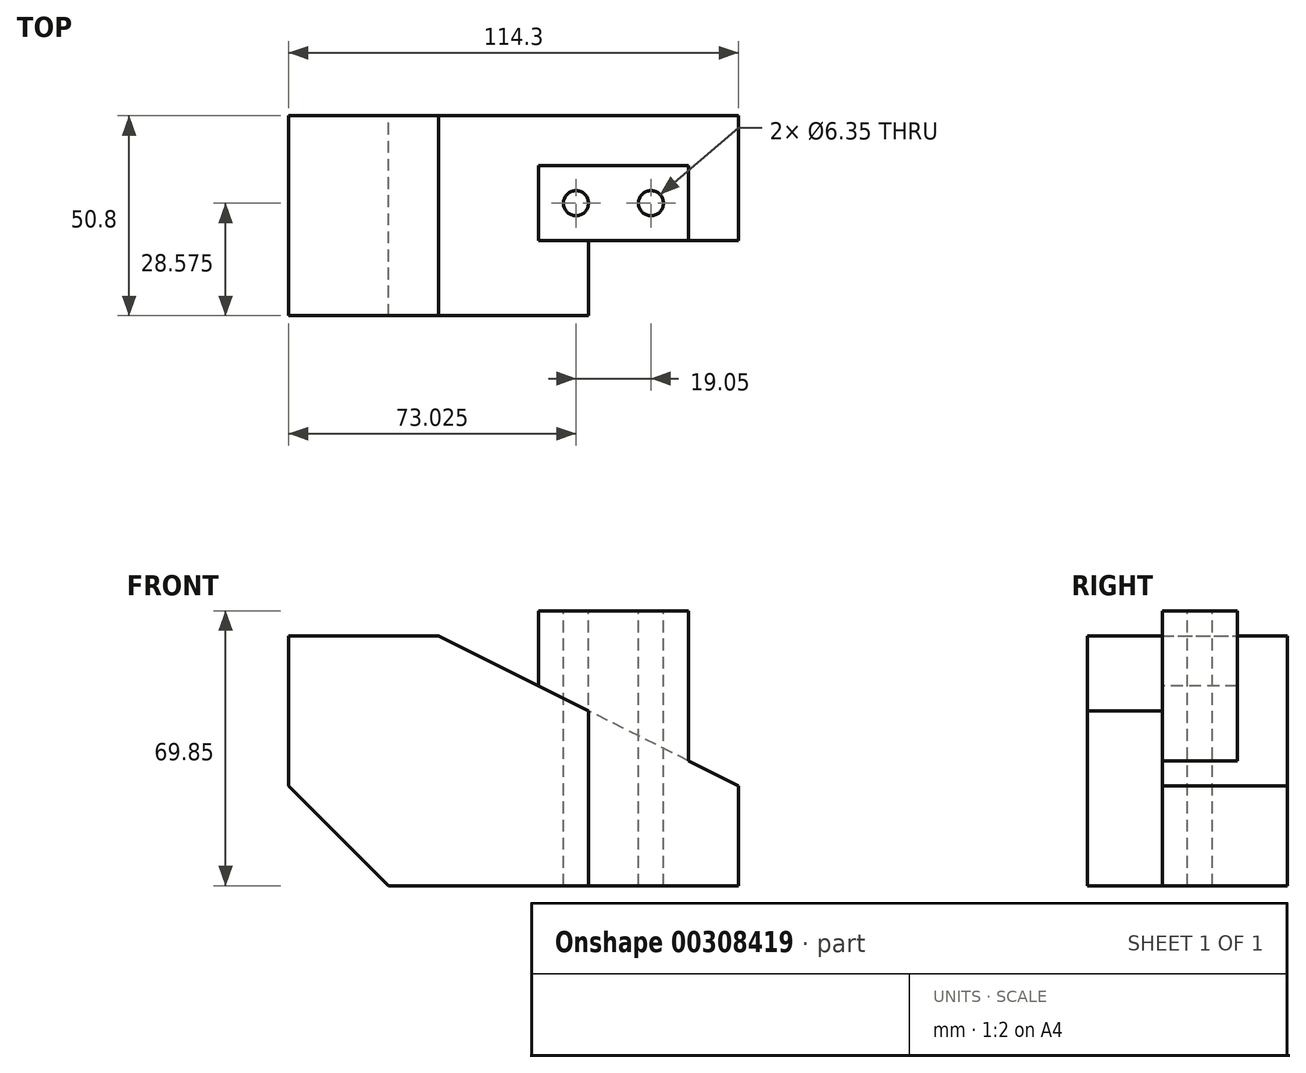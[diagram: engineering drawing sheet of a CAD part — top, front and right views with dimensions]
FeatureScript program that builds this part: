
annotation { "Feature Type Name" : "Feature", "Feature Type Description" : "" }
export const myFeature = defineFeature(function(context is Context, id is Id, definition is map)
    precondition{}
    {
        {
            var Q0;
            Q0=qCreatedBy(makeId("Front.planeOp"),FACE);
            var sketch = newSketch(context, id + "F0", { "sketchPlane" : qUnion([Q0])});
            skLineSegment(sketch, "E0", {"start": v(-63.5, 38.1) * mm, "end": v(-63.5, 0) * mm});
            skLineSegment(sketch, "E1", {"start": v(-63.5, 0) * mm, "end": v(-38.1, -25.4) * mm});
            skLineSegment(sketch, "E2", {"start": v(-38.1, -25.4) * mm, "end": v(50.8, -25.4) * mm});
            skLineSegment(sketch, "E3", {"start": v(50.8, -25.4) * mm, "end": v(50.8, 0) * mm});
            skLineSegment(sketch, "E4", {"start": v(50.8, 0) * mm, "end": v(-25.4, 38.1) * mm});
            skLineSegment(sketch, "E5", {"start": v(-25.4, 38.1) * mm, "end": v(-63.5, 38.1) * mm});
            skSolve(sketch);
        }
        {
            var Q0;
            Q0 = qSketchRegion(id + "F0", true);
            extrude(context, id + "F1", {"entities" : qUnion([Q0]), "depth" : 50.8 * mm});
        }
        {
            var Q0;
            Q0=makeQuery(id+"F1.opExtrude","SWEPT_FACE",FACE,{"disambiguationData":[OSD([sQuery(id+"F0.wireOp",EDGE,"E5")])]});
            var sketch = newSketch(context, id + "F2", { "sketchPlane" : qUnion([Q0])});
            skLineSegment(sketch, "E6.bottom", {"start": v(50.8, -50.8) * mm, "end": v(12.7, -50.8) * mm});
            skLineSegment(sketch, "E6.top", {"start": v(50.8, -31.75) * mm, "end": v(12.7, -31.75) * mm});
            skLineSegment(sketch, "E6.left", {"start": v(50.8, -50.8) * mm, "end": v(50.8, -31.75) * mm});
            skLineSegment(sketch, "E6.right", {"start": v(12.7, -50.8) * mm, "end": v(12.7, -31.75) * mm});
            skSolve(sketch);
        }
        {
            var Q0;
            Q0=makeQuery(id+"F2.imprint","IMPRINT",FACE,{"disambiguationData":[TD([[makeQuery(id+"F2.imprint","IMPRINT",EDGE,{"derivedFrom":sQuery(id+"F2.wireOp",EDGE,"E6.bottom")}),-1.0]])]});
            extrude(context, id + "F3", {"entities" : qUnion([Q0]), "operationType" : NewBodyOperationType.REMOVE, "endBound" : BoundingType.THROUGH_ALL, "oppositeDirection" : true, "depth" : 25.4 * mm});
        }
        {
            var Q0;
            Q0=makeQuery(id+"F3.boolean.opBoolean","COPY",FACE,{"derivedFrom":makeQuery(id+"F3.opExtrude","SWEPT_FACE",FACE,{"disambiguationData":[OSD([sQuery(id+"F2.wireOp",EDGE,"E6.right")])]})});
            cPlane(context, id + "F4", {"entities" : qUnion([Q0]), "cplaneType" : CPlaneType.OFFSET, "offset" : 25.4 * mm, "width" : 152.4 * mm, "height" : 152.4 * mm});
        }
        {
            var Q0;
            Q0=qCreatedBy(id+"F4.planeOp",FACE);
            var sketch = newSketch(context, id + "F5", { "sketchPlane" : qUnion([Q0])});
            skLineSegment(sketch, "E7.bottom", {"start": v(-31.75, 44.45) * mm, "end": v(-12.7, 44.45) * mm});
            skLineSegment(sketch, "E7.top", {"start": v(-31.75, 6.35) * mm, "end": v(-12.7, 6.35) * mm});
            skLineSegment(sketch, "E7.left", {"start": v(-31.75, 44.45) * mm, "end": v(-31.75, 6.35) * mm});
            skLineSegment(sketch, "E7.right", {"start": v(-12.7, 44.45) * mm, "end": v(-12.7, 6.35) * mm});
            skSolve(sketch);
        }
        {
            var Q0;
            Q0 = qSketchRegion(id + "F5", true);
            extrude(context, id + "F6", {"entities" : qUnion([Q0]), "operationType" : NewBodyOperationType.ADD, "oppositeDirection" : true, "depth" : 38.1 * mm});
        }
        {
            var Q0;
            Q0=makeQuery(id+"F6.opExtrude","SWEPT_FACE",FACE,{"disambiguationData":[OSD([sQuery(id+"F5.wireOp",EDGE,"E7.bottom")])]});
            var sketch = newSketch(context, id + "F7", { "sketchPlane" : qUnion([Q0])});
            skCircle(sketch, "E8", {"center": v(9.53, -22.23) * mm, "radius": 3.18 * mm});
            skCircle(sketch, "E9", {"center": v(28.58, -22.22) * mm, "radius": 3.18 * mm});
            skSolve(sketch);
        }
        {
            var Q0;
            Q0 = qSketchRegion(id + "F7", true);
            extrude(context, id + "F8", {"entities" : qUnion([Q0]), "operationType" : NewBodyOperationType.REMOVE, "endBound" : BoundingType.THROUGH_ALL, "oppositeDirection" : true, "depth" : 25.4 * mm});
        }
    });
